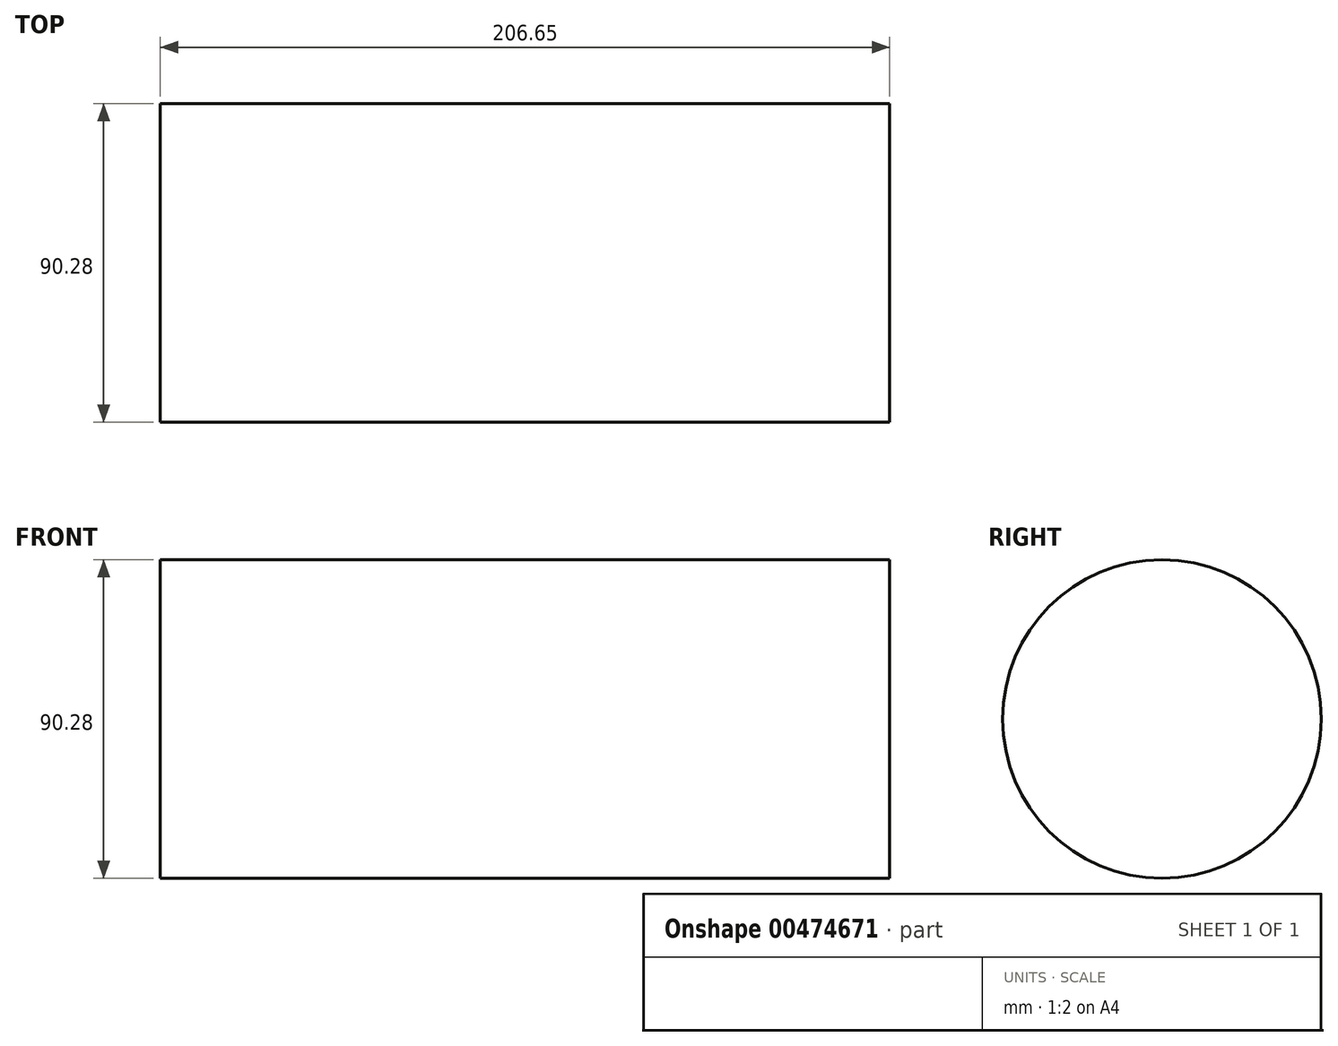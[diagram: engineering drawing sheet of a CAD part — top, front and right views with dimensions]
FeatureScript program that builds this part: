
annotation { "Feature Type Name" : "Feature", "Feature Type Description" : "" }
export const myFeature = defineFeature(function(context is Context, id is Id, definition is map)
    precondition{}
    {
        {
            var Q0;
            Q0=qCreatedBy(makeId("Front.planeOp"),FACE);
            var sketch = newSketch(context, id + "F0", { "sketchPlane" : qUnion([Q0])});
            skLineSegment(sketch, "E0.bottom", {"start": v(-73.38, 45.14) * mm, "end": v(133.27, 45.14) * mm});
            skLineSegment(sketch, "E0.top", {"start": v(-73.38, 0) * mm, "end": v(133.27, 0) * mm});
            skLineSegment(sketch, "E0.left", {"start": v(-73.38, 45.14) * mm, "end": v(-73.38, 0) * mm});
            skLineSegment(sketch, "E0.right", {"start": v(133.27, 45.14) * mm, "end": v(133.27, 0) * mm});
            skSolve(sketch);
        }
        {
            var Q0;
            Q0=makeQuery(id+"F0.imprint","IMPRINT",FACE,{"disambiguationData":[TD([[makeQuery(id+"F0.imprint","IMPRINT",EDGE,{"derivedFrom":sQuery(id+"F0.wireOp",EDGE,"E0.bottom")}),-1.0]])]});
            var Q1;
            Q1=sQuery(id+"F0.wireOp",EDGE,"E0.top");
            revolve(context, id + "F1", {"entities" : qUnion([Q0]), "axis" : qUnion([Q1]), "revolveType" : RevolveType.FULL});
        }
    });
